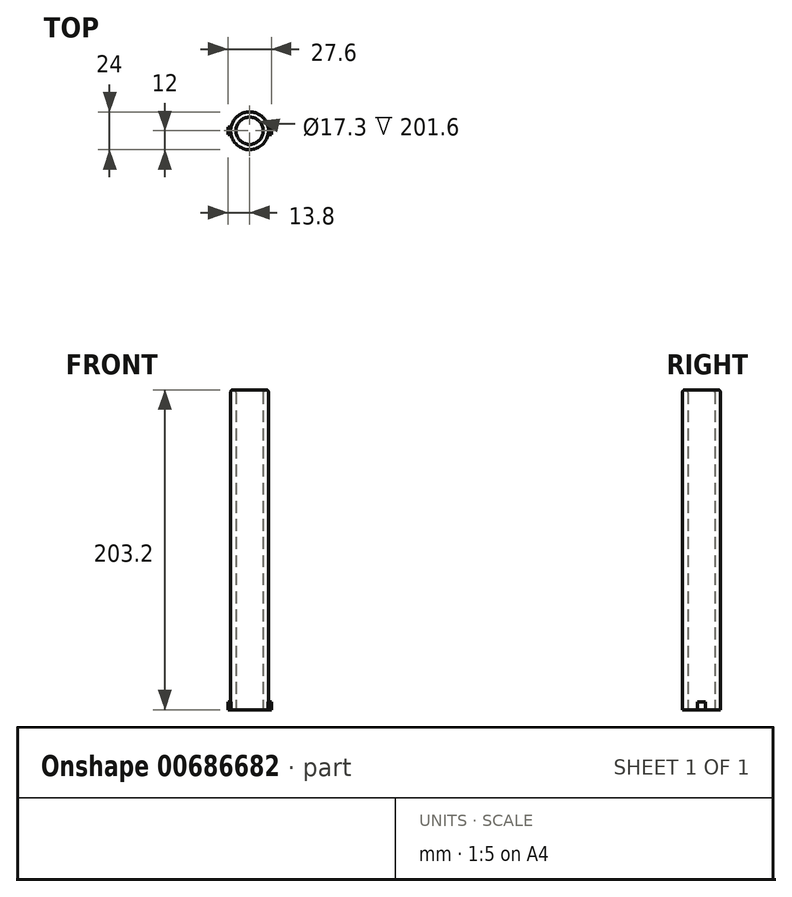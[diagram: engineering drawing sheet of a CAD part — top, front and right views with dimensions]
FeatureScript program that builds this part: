
annotation { "Feature Type Name" : "Feature", "Feature Type Description" : "" }
export const myFeature = defineFeature(function(context is Context, id is Id, definition is map)
    precondition{}
    {
        {
            var Q0;
            Q0=qCreatedBy(makeId("Top.planeOp"),FACE);
            var sketch = newSketch(context, id + "F0", { "sketchPlane" : qUnion([Q0])});
            skCircle(sketch, "E0", {"center": v(0, 0) * mm, "radius": 8.65 * mm});
            skCircle(sketch, "E1", {"center": v(0, 0) * mm, "radius": 12 * mm});
            skLineSegment(sketch, "E2.bottom", {"start": v(-11.74, 2.5) * mm, "end": v(-13.8, 2.5) * mm});
            skLineSegment(sketch, "E2.top", {"start": v(-11.74, -2.43) * mm, "end": v(-13.8, -2.43) * mm});
            skLineSegment(sketch, "E2.left", {"start": v(-11.74, 2.5) * mm, "end": v(-11.74, -2.43) * mm});
            skLineSegment(sketch, "E2.right", {"start": v(-13.8, 2.5) * mm, "end": v(-13.8, -2.43) * mm});
            skLineSegment(sketch, "E3.MirrorCS", {"start": v(11.74, 2.5) * mm, "end": v(13.8, 2.5) * mm});
            skLineSegment(sketch, "E4.MirrorCS", {"start": v(11.74, 2.5) * mm, "end": v(11.74, -2.43) * mm});
            skLineSegment(sketch, "E5.MirrorCS", {"start": v(13.8, 2.5) * mm, "end": v(13.8, -2.43) * mm});
            skLineSegment(sketch, "E6.MirrorCS", {"start": v(11.74, -2.43) * mm, "end": v(13.8, -2.43) * mm});
            skSolve(sketch);
        }
        {
            var Q0;
            Q0=makeQuery(id+"F0.imprint","IMPRINT",FACE,{"disambiguationData":[TD([[makeQuery(id+"F0.imprint","IMPRINT",EDGE,{"derivedFrom":sQuery(id+"F0.wireOp",EDGE,"E0")}),-1.0]])]});
            var Q1;
            {var subQ0=sQuery(id+"F0.wireOp",EDGE,"E2.left");Q1=makeQuery(id+"F0.imprint","IMPRINT",FACE,{"disambiguationData":[TD([[makeQuery(id+"F0.imprint","IMPRINT",EDGE,{"derivedFrom":subQ0}),-1.0]])]});}
            var Q2;
            {var subQ0=sQuery(id+"F0.wireOp",EDGE,"E4.MirrorCS");Q2=makeQuery(id+"F0.imprint","IMPRINT",FACE,{"disambiguationData":[TD([[makeQuery(id+"F0.imprint","IMPRINT",EDGE,{"derivedFrom":subQ0}),1.0]])]});}
            extrude(context, id + "F1", {"entities" : qUnion([Q0, Q1, Q2]), "depth" : 203.2 * mm, "offsetDistance" : 25 * mm});
        }
        {
            var Q0;
            Q0=makeQuery(id+"F1.opExtrude","CAP_EDGE",EDGE,{"disambiguationData":[OSD([sQuery(id+"F0.wireOp",EDGE,"E1")])],"isStart":false});
            var Q1;
            Q1=makeQuery(id+"F1.opExtrude","CAP_EDGE",EDGE,{"disambiguationData":[OSD([sQuery(id+"F0.wireOp",EDGE,"E0")])],"isStart":false});
            fillet(context, id + "F2", {"entities" : qUnion([Q0, Q1]), "radius" : 1.6 * mm, "tangentPropagation" : true, "allowEdgeOverflow" : false});
        }
        {
            var Q0;
            {var subQ0=sQuery(id+"F0.wireOp",EDGE,"E3.MirrorCS");Q0=makeQuery(id+"F0.imprint","IMPRINT",FACE,{"disambiguationData":[TD([[makeQuery(id+"F0.imprint","IMPRINT",EDGE,{"derivedFrom":subQ0}),-1.0]])]});}
            var Q1;
            {var subQ0=sQuery(id+"F0.wireOp",EDGE,"E2.bottom");Q1=makeQuery(id+"F0.imprint","IMPRINT",FACE,{"disambiguationData":[TD([[makeQuery(id+"F0.imprint","IMPRINT",EDGE,{"derivedFrom":subQ0}),1.0]])]});}
            extrude(context, id + "F3", {"entities" : qUnion([Q0, Q1]), "operationType" : NewBodyOperationType.ADD, "depth" : 5 * mm, "offsetDistance" : 25 * mm});
        }
    });
